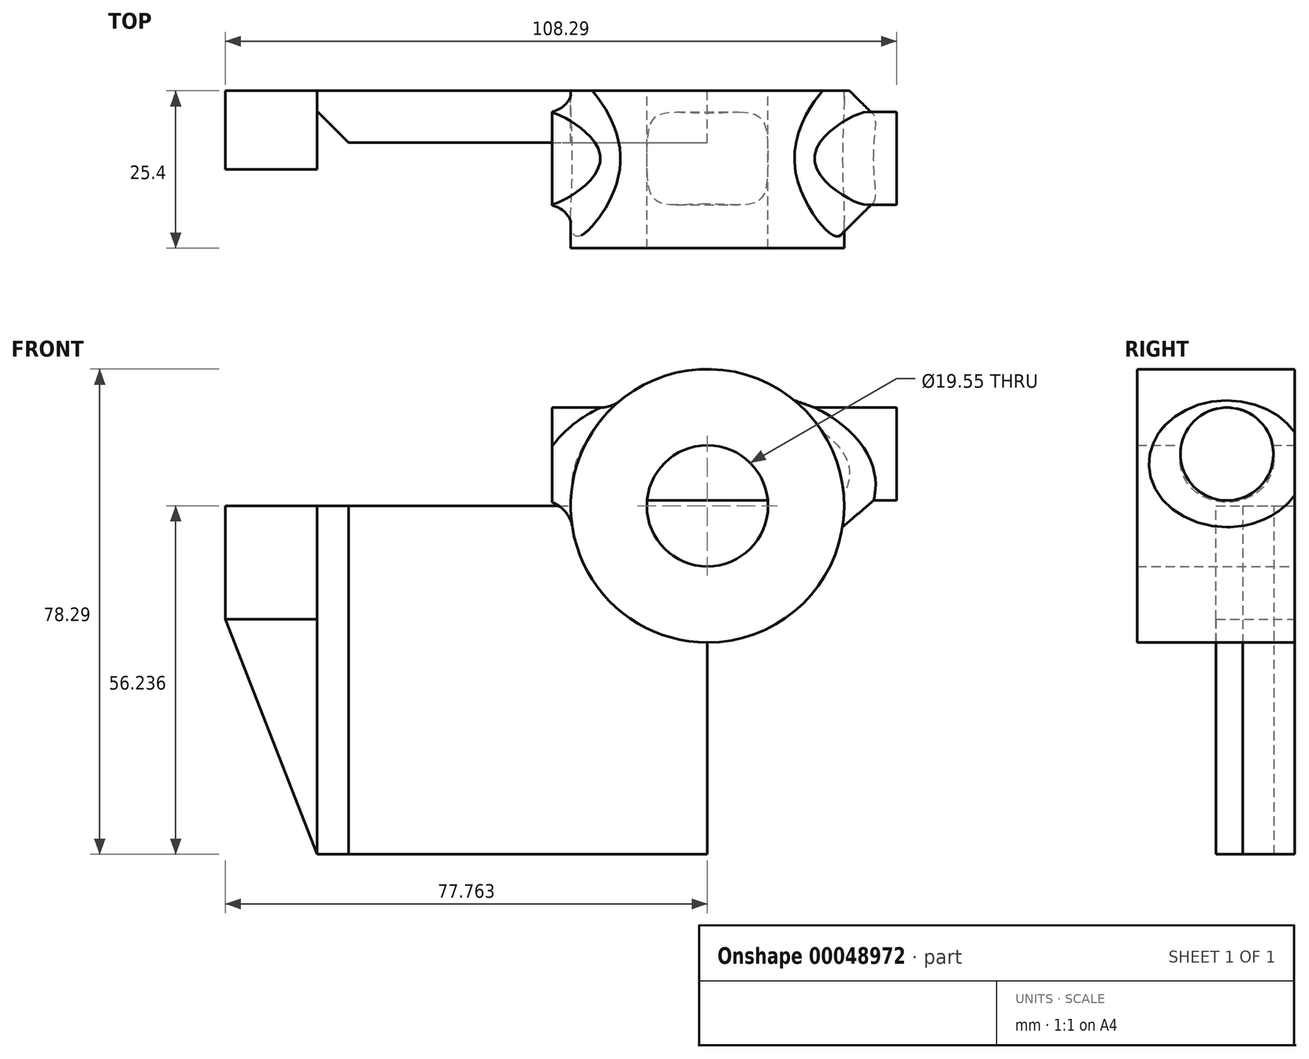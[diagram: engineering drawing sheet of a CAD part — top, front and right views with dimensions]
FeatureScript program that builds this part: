
annotation { "Feature Type Name" : "Feature", "Feature Type Description" : "" }
export const myFeature = defineFeature(function(context is Context, id is Id, definition is map)
    precondition{}
    {
        {
            var Q0;
            Q0=qCreatedBy(makeId("Front.planeOp"),FACE);
            var sketch = newSketch(context, id + "F0", { "sketchPlane" : qUnion([Q0])});
            skLineSegment(sketch, "E0.bottom", {"start": v(-37.92, -30.53) * mm, "end": v(25.06, -30.53) * mm});
            skLineSegment(sketch, "E0.top", {"start": v(-37.92, 25.7) * mm, "end": v(25.06, 25.7) * mm});
            skLineSegment(sketch, "E0.left", {"start": v(-37.92, -30.53) * mm, "end": v(-37.92, 25.7) * mm});
            skLineSegment(sketch, "E0.right", {"start": v(25.06, -30.53) * mm, "end": v(25.06, 25.7) * mm});
            skLineSegment(sketch, "E1.bottom", {"start": v(-37.92, 25.7) * mm, "end": v(-52.7, 25.7) * mm});
            skLineSegment(sketch, "E1.top", {"start": v(-37.92, 7.4) * mm, "end": v(-52.7, 7.4) * mm});
            skLineSegment(sketch, "E1.left", {"start": v(-37.92, 25.7) * mm, "end": v(-37.92, 7.4) * mm});
            skLineSegment(sketch, "E1.right", {"start": v(-52.7, 25.7) * mm, "end": v(-52.7, 7.4) * mm});
            skLineSegment(sketch, "E2", {"start": v(-52.7, 7.4) * mm, "end": v(-37.92, -30.53) * mm});
            skCircle(sketch, "E3", {"center": v(25.06, 25.7) * mm, "radius": 22.05 * mm});
            skCircle(sketch, "E4", {"center": v(25.06, 25.7) * mm, "radius": 9.77 * mm});
            skSolve(sketch);
        }
        {
            var Q0;
            {var subQ0=sQuery(id+"F0.wireOp",EDGE,"E3");var subQ3=sQuery(id+"F0.wireOp",EDGE,"E0.top");var subQ4=makeQuery(id+"F0.imprint","INTERSECT",VERTEX,{"derivedFrom":[subQ3,subQ0]});Q0=makeQuery(id+"F0.imprint","IMPRINT",FACE,{"disambiguationData":[TD([[makeQuery(id+"F0.imprint","IMPRINT",EDGE,{"disambiguationData":[TD([[subQ4,-1.0]])],"derivedFrom":subQ3}),1.0]])]});}
            var Q1;
            {var subQ3=sQuery(id+"F0.wireOp",EDGE,"E0.top");var subQ5=sQuery(id+"F0.wireOp",EDGE,"E3");var subQ7=makeQuery(id+"F0.imprint","INTERSECT",VERTEX,{"derivedFrom":[subQ3,subQ5]});Q1=makeQuery(id+"F0.imprint","IMPRINT",FACE,{"disambiguationData":[TD([[makeQuery(id+"F0.imprint","IMPRINT",EDGE,{"disambiguationData":[TD([[subQ7,-1.0]])],"derivedFrom":subQ3}),-1.0]])]});}
            extrude(context, id + "F1", {"entities" : qUnion([Q0, Q1]), "depth" : 25.4 * mm});
        }
        {
            var Q0;
            Q0=makeQuery(id+"F0.imprint","IMPRINT",FACE,{"disambiguationData":[TD([[makeQuery(id+"F0.imprint","IMPRINT",EDGE,{"derivedFrom":sQuery(id+"F0.wireOp",EDGE,"E1.bottom")}),1.0]])]});
            extrude(context, id + "F2", {"entities" : qUnion([Q0]), "depth" : 12.7 * mm});
        }
        {
            var Q0;
            {var subQ6=sQuery(id+"F0.wireOp",EDGE,"E0.bottom");Q0=makeQuery(id+"F0.imprint","IMPRINT",FACE,{"disambiguationData":[TD([[makeQuery(id+"F0.imprint","IMPRINT",EDGE,{"derivedFrom":subQ6}),1.0]])]});}
            extrude(context, id + "F3", {"entities" : qUnion([Q0]), "depth" : 8.38 * mm});
        }
        {
            var Q0;
            Q0=makeQuery(id+"F0.imprint","IMPRINT",FACE,{"disambiguationData":[TD([[makeQuery(id+"F0.imprint","IMPRINT",EDGE,{"derivedFrom":sQuery(id+"F0.wireOp",EDGE,"E0.left")}),1.0]])]});
            extrude(context, id + "F4", {"entities" : qUnion([Q0]), "depth" : 12.7 * mm});
        }
        {
            var Q0;
            Q0=qCreatedBy(makeId("Right.planeOp"),FACE);
            var sketch = newSketch(context, id + "F5", { "sketchPlane" : qUnion([Q0])});
            skCircle(sketch, "E5", {"center": v(-10.93, 34.06) * mm, "radius": 7.5 * mm});
            skLineSegment(sketch, "E6", {"start": v(-10.93, 34.06) * mm, "end": v(-10.93, 50.39) * mm});
            skSolve(sketch);
        }
        {
            var Q0;
            Q0=qCreatedBy(makeId("Front.planeOp"),FACE);
            var sketch = newSketch(context, id + "F6", { "sketchPlane" : qUnion([Q0])});
            skPoint(sketch, "E7.0", {"position": v(0, 34.06) * mm});
            skPoint(sketch, "E8.0", {"position": v(0, 0) * mm});
            skLineSegment(sketch, "E9", {"start": v(0, 34.06) * mm, "end": v(55.59, 34.06) * mm});
            skSolve(sketch);
        }
        {
            var Q0;
            Q0=makeQuery(id+"F5.imprint","IMPRINT",FACE,{"disambiguationData":[TD([[makeQuery(id+"F5.imprint","IMPRINT",EDGE,{"derivedFrom":sQuery(id+"F5.wireOp",EDGE,"E5")}),1.0]])]});
            var Q1;
            Q1=sQuery(id+"F6.wireOp",EDGE,"E9");
            sweep(context, id + "F7", {"operationType" : NewBodyOperationType.ADD, "profiles" : qUnion([Q0]), "path" : qUnion([Q1])});
        }
        {
            var Q0;
            Q0=makeQuery(id+"F7.boolean.opBoolean","INTERSECT",EDGE,{"disambiguationData":[OD(0.0)],"derivedFrom":[makeQuery(id+"F1.opExtrude","SWEPT_FACE",FACE,{"disambiguationData":[OSD([sQuery(id+"F0.wireOp",EDGE,"E3")])]}),makeQuery(id+"F7.opSweep","SWEPT_FACE",FACE,{"disambiguationData":[OSD([sQuery(id+"F5.wireOp",EDGE,"E5"),sQuery(id+"F6.wireOp",EDGE,"E9")])]})]});
            fillet(context, id + "F8", {"entities" : qUnion([Q0]), "radius" : 5.08 * mm, "tangentPropagation" : true, "allowEdgeOverflow" : false});
        }
        {
            var Q0;
            Q0=makeQuery(id+"F7.boolean.opBoolean","INTERSECT",EDGE,{"disambiguationData":[OD(1.0)],"derivedFrom":[makeQuery(id+"F1.opExtrude","SWEPT_FACE",FACE,{"disambiguationData":[OSD([sQuery(id+"F0.wireOp",EDGE,"E3")])]}),makeQuery(id+"F7.opSweep","SWEPT_FACE",FACE,{"disambiguationData":[OSD([sQuery(id+"F5.wireOp",EDGE,"E5"),sQuery(id+"F6.wireOp",EDGE,"E9")])]})]});
            chamfer(context, id + "F9", {"entities" : qUnion([Q0]), "width" : 5.08 * mm, "tangentPropagation" : true});
        }
        {
            var Q0;
            Q0=makeQuery(id+"F3.opExtrude","CAP_EDGE",EDGE,{"disambiguationData":[OSD([sQuery(id+"F0.wireOp",EDGE,"E0.left"),sQuery(id+"F0.wireOp",EDGE,"E1.left")])],"isStart":false});
            chamfer(context, id + "F10", {"entities" : qUnion([Q0]), "width" : 5.08 * mm, "tangentPropagation" : true});
        }
    });
